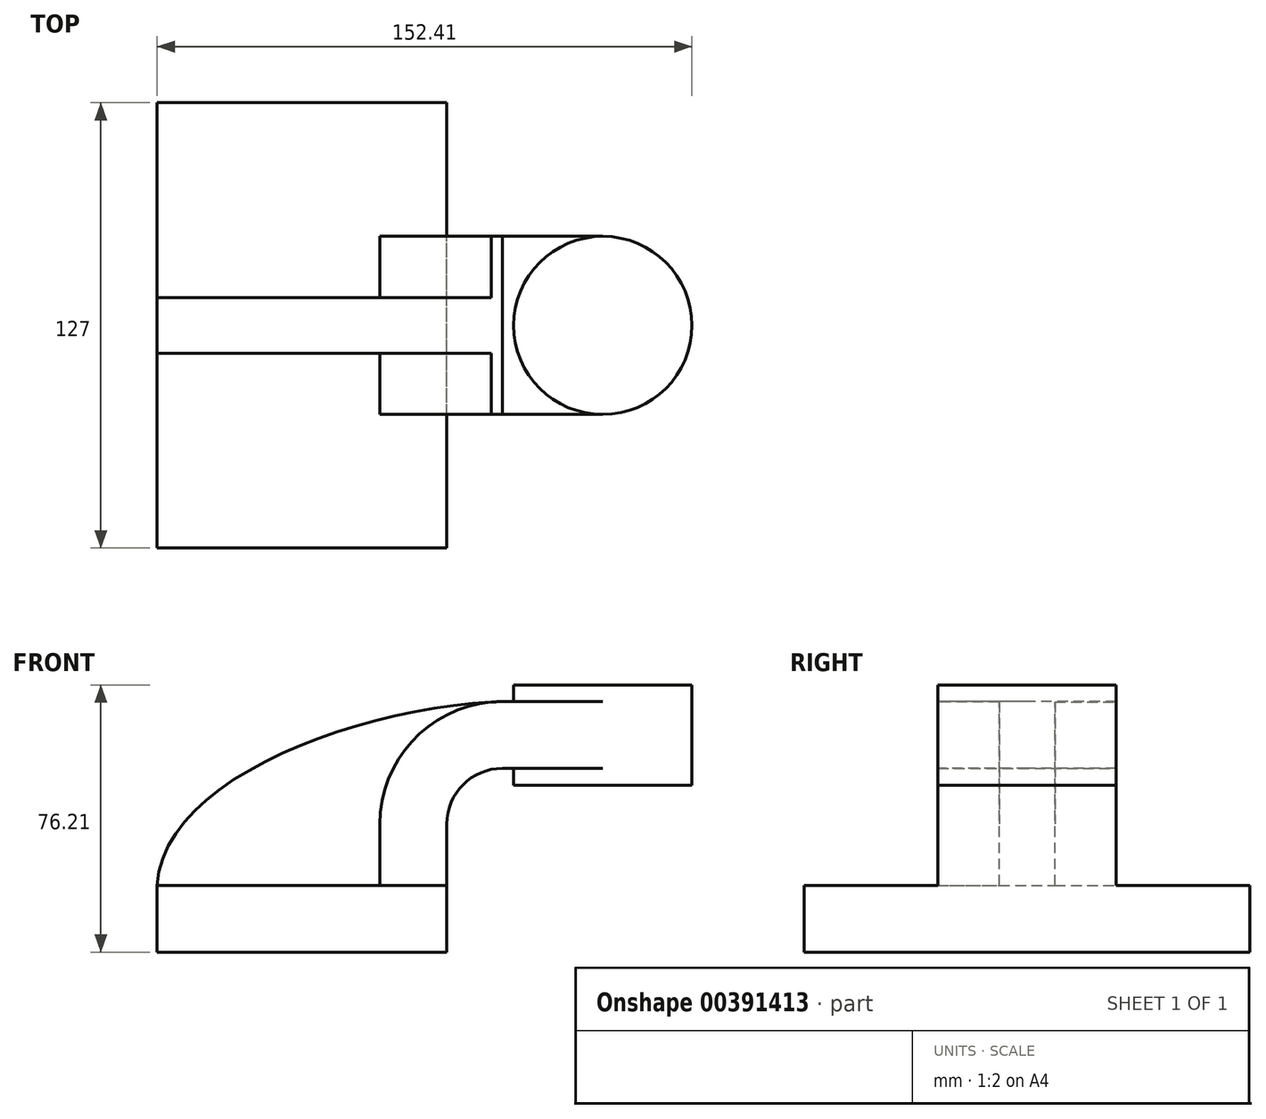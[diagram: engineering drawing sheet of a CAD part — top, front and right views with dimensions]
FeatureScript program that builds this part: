
annotation { "Feature Type Name" : "Feature", "Feature Type Description" : "" }
export const myFeature = defineFeature(function(context is Context, id is Id, definition is map)
    precondition{}
    {
        {
            var Q0;
            Q0=qCreatedBy(makeId("Front.planeOp"),FACE);
            var sketch = newSketch(context, id + "F0", { "sketchPlane" : qUnion([Q0])});
            skLineSegment(sketch, "E0.rect.bottom", {"start": v(-41.28, 9.52) * mm, "end": v(41.28, 9.52) * mm});
            skLineSegment(sketch, "E0.rect.top", {"start": v(-41.28, -9.52) * mm, "end": v(41.28, -9.52) * mm});
            skLineSegment(sketch, "E0.rect.left", {"start": v(-41.28, 9.52) * mm, "end": v(-41.28, -9.52) * mm});
            skLineSegment(sketch, "E0.rect.right", {"start": v(41.28, 9.52) * mm, "end": v(41.28, -9.52) * mm});
            skPoint(sketch, "E0.rect.middle", {"position": v(0, 0) * mm});
            skLineSegment(sketch, "E1", {"start": v(41.28, 9.52) * mm, "end": v(41.28, 27) * mm});
            skArc(sketch, "E2", {"start": v(41.28, 27) * mm, "mid": v(45.92, 38.23) * mm, "end": v(57.15, 42.88) * mm});
            skLineSegment(sketch, "E3", {"start": v(57.15, 42.88) * mm, "end": v(85.72, 42.88) * mm});
            skLineSegment(sketch, "E4.rect.bottom", {"start": v(60.32, 38.1) * mm, "end": v(111.12, 38.1) * mm});
            skLineSegment(sketch, "E4.rect.top", {"start": v(60.32, 66.68) * mm, "end": v(111.12, 66.68) * mm});
            skLineSegment(sketch, "E4.rect.left", {"start": v(60.32, 38.1) * mm, "end": v(60.32, 66.68) * mm});
            skLineSegment(sketch, "E4.rect.right", {"start": v(111.13, 38.1) * mm, "end": v(111.12, 66.68) * mm});
            skPoint(sketch, "E4.rect.middle", {"position": v(85.72, 52.39) * mm});
            skLineSegment(sketch, "E5.0", {"start": v(57.15, 61.93) * mm, "end": v(85.72, 61.93) * mm});
            skArc(sketch, "E5.1", {"start": v(22.23, 27) * mm, "mid": v(32.45, 51.7) * mm, "end": v(57.15, 61.93) * mm});
            skLineSegment(sketch, "E5.2", {"start": v(22.23, 9.52) * mm, "end": v(22.23, 27) * mm});
            skLineSegment(sketch, "E6", {"start": v(85.72, 38.1) * mm, "end": v(85.72, 66.68) * mm});
            skFitSpline(sketch, "E7", {"points": [v(-41.28, 9.53) * mm, v(57.15, 61.93) * mm], "startDerivative": vector(5.2, 92.34) * mm, "endDerivative": vector(120.92, 4.22) * mm});
            skSolve(sketch);
        }
        {
            var Q0;
            Q0=makeQuery(id+"F0.imprint","IMPRINT",FACE,{"disambiguationData":[TD([[makeQuery(id+"F0.imprint","IMPRINT",EDGE,{"derivedFrom":sQuery(id+"F0.wireOp",EDGE,"E0.rect.top")}),1.0]])]});
            extrude(context, id + "F1", {"entities" : qUnion([Q0]), "endBound" : BoundingType.SYMMETRIC, "depth" : 127 * mm});
        }
        {
            var Q0;
            {var subQ9=sQuery(id+"F0.wireOp",EDGE,"E1");Q0=makeQuery(id+"F0.imprint","IMPRINT",FACE,{"disambiguationData":[TD([[makeQuery(id+"F0.imprint","IMPRINT",EDGE,{"derivedFrom":subQ9}),1.0]])]});}
            var Q1;
            {var subQ0=sQuery(id+"F0.wireOp",EDGE,"E6");var subQ1=sQuery(id+"F0.wireOp",EDGE,"E3");var subQ2=makeQuery(id+"F0.imprint","INTERSECT",VERTEX,{"derivedFrom":[subQ1,subQ0]});Q1=makeQuery(id+"F0.imprint","IMPRINT",FACE,{"disambiguationData":[TD([[makeQuery(id+"F0.imprint","IMPRINT",EDGE,{"disambiguationData":[TD([[subQ2,1.0]])],"derivedFrom":subQ1}),1.0]])]});}
            extrude(context, id + "F2", {"entities" : qUnion([Q0, Q1]), "operationType" : NewBodyOperationType.ADD, "endBound" : BoundingType.SYMMETRIC, "depth" : 50.8 * mm});
        }
        {
            var Q0;
            {var subQ3=sQuery(id+"F0.wireOp",EDGE,"E5.2");Q0=makeQuery(id+"F0.imprint","IMPRINT",FACE,{"disambiguationData":[TD([[makeQuery(id+"F0.imprint","IMPRINT",EDGE,{"derivedFrom":subQ3}),1.0]])]});}
            extrude(context, id + "F3", {"entities" : qUnion([Q0]), "operationType" : NewBodyOperationType.ADD, "endBound" : BoundingType.SYMMETRIC, "depth" : 15.88 * mm});
        }
        {
            var Q0;
            {var subQ5=sQuery(id+"F0.wireOp",EDGE,"E4.rect.right");Q0=makeQuery(id+"F0.imprint","IMPRINT",FACE,{"disambiguationData":[TD([[makeQuery(id+"F0.imprint","IMPRINT",EDGE,{"derivedFrom":subQ5}),1.0]])]});}
            var Q1;
            Q1=sQuery(id+"F0.wireOp",EDGE,"E6");
            revolve(context, id + "F4", {"operationType" : NewBodyOperationType.ADD, "entities" : qUnion([Q0]), "axis" : qUnion([Q1]), "revolveType" : RevolveType.FULL});
        }
    });
